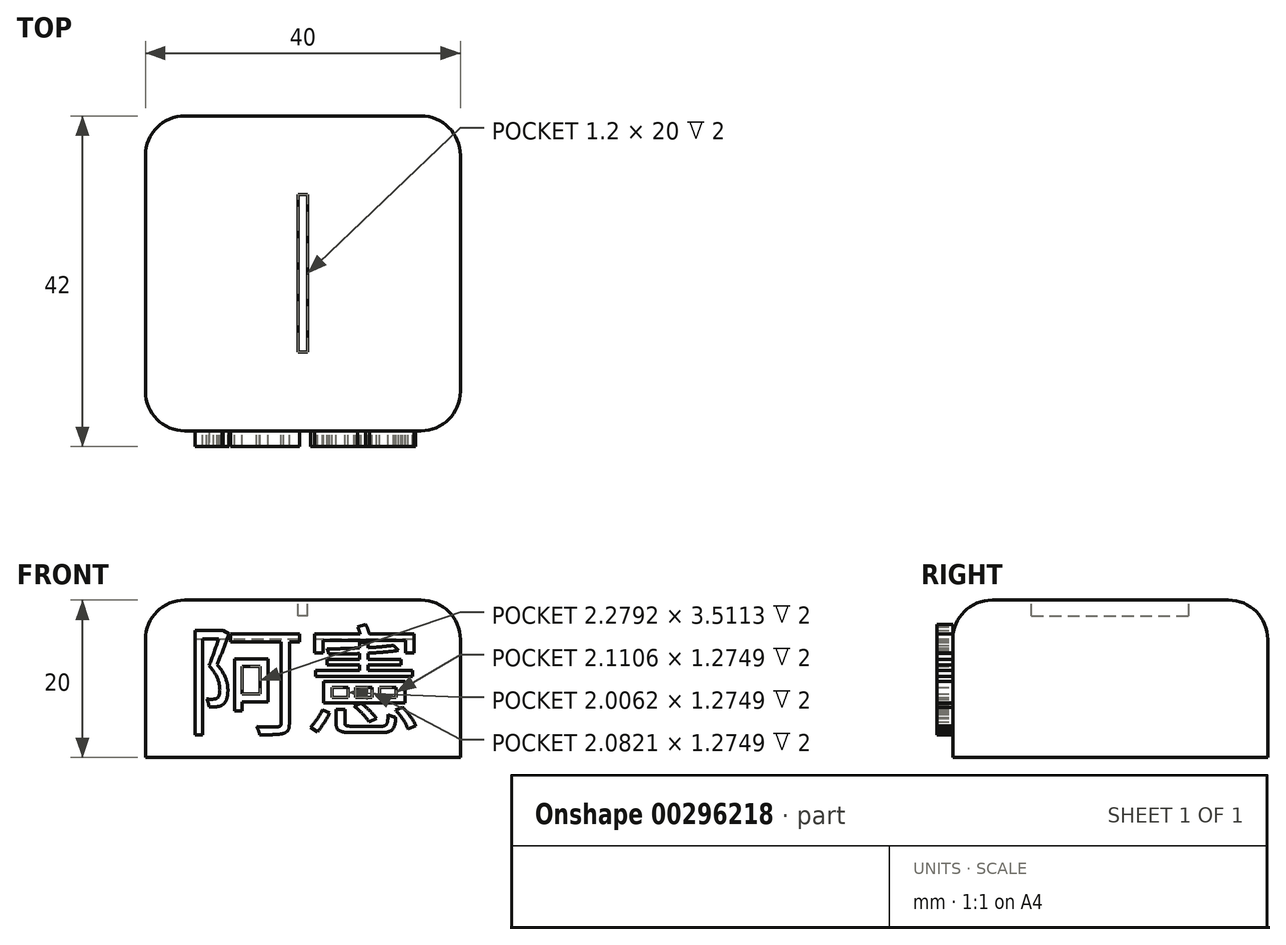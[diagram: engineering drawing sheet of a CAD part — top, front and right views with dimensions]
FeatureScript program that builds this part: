
annotation { "Feature Type Name" : "Feature", "Feature Type Description" : "" }
export const myFeature = defineFeature(function(context is Context, id is Id, definition is map)
    precondition{}
    {
        {
            var Q0;
            Q0=qCreatedBy(makeId("Top.planeOp"),FACE);
            var sketch = newSketch(context, id + "F0", { "sketchPlane" : qUnion([Q0])});
            skLineSegment(sketch, "E0.bottom", {"start": v(20, -20) * mm, "end": v(-20, -20) * mm});
            skLineSegment(sketch, "E0.top", {"start": v(20, 20) * mm, "end": v(-20, 20) * mm});
            skLineSegment(sketch, "E0.left", {"start": v(20, -20) * mm, "end": v(20, 20) * mm});
            skLineSegment(sketch, "E0.right", {"start": v(-20, -20) * mm, "end": v(-20, 20) * mm});
            skPoint(sketch, "E0.middle", {"position": v(0, 0) * mm});
            skLineSegment(sketch, "E1.bottom", {"start": v(0.6, -10) * mm, "end": v(-0.6, -10) * mm});
            skLineSegment(sketch, "E1.top", {"start": v(0.6, 10) * mm, "end": v(-0.6, 10) * mm});
            skLineSegment(sketch, "E1.left", {"start": v(0.6, -10) * mm, "end": v(0.6, 10) * mm});
            skLineSegment(sketch, "E1.right", {"start": v(-0.6, -10) * mm, "end": v(-0.6, 10) * mm});
            skSolve(sketch);
        }
        {
            var Q0;
            Q0=makeQuery(id+"F0.imprint","IMPRINT",FACE,{"disambiguationData":[TD([[makeQuery(id+"F0.imprint","IMPRINT",EDGE,{"derivedFrom":sQuery(id+"F0.wireOp",EDGE,"E0.bottom")}),-1.0]])]});
            var Q1;
            Q1=makeQuery(id+"F0.imprint","IMPRINT",FACE,{"disambiguationData":[TD([[makeQuery(id+"F0.imprint","IMPRINT",EDGE,{"derivedFrom":sQuery(id+"F0.wireOp",EDGE,"E1.bottom")}),-1.0]])]});
            extrude(context, id + "F1", {"entities" : qUnion([Q0, Q1]), "oppositeDirection" : true, "depth" : 20 * mm});
        }
        {
            var Q0;
            Q0=makeQuery(id+"F0.imprint","IMPRINT",FACE,{"disambiguationData":[TD([[makeQuery(id+"F0.imprint","IMPRINT",EDGE,{"derivedFrom":sQuery(id+"F0.wireOp",EDGE,"E1.bottom")}),-1.0]])]});
            extrude(context, id + "F2", {"entities" : qUnion([Q0]), "operationType" : NewBodyOperationType.REMOVE, "oppositeDirection" : true, "depth" : 2 * mm});
        }
        {
            var Q0;
            Q0=makeQuery(id+"F2.boolean.opBoolean","COPY",EDGE,{"derivedFrom":makeQuery(id+"F2.opExtrude","CAP_EDGE",EDGE,{"disambiguationData":[OSD([sQuery(id+"F0.wireOp",EDGE,"E1.left")])],"isStart":true})});
            var Q1;
            Q1=makeQuery(id+"F2.boolean.opBoolean","COPY",EDGE,{"derivedFrom":makeQuery(id+"F2.opExtrude","CAP_EDGE",EDGE,{"disambiguationData":[OSD([sQuery(id+"F0.wireOp",EDGE,"E1.right")])],"isStart":true})});
            var Q2;
            Q2=makeQuery(id+"F1.opExtrude","SWEPT_EDGE",EDGE,{"disambiguationData":[OSD([sQuery(id+"F0.wireOp",EDGE,"E0.bottom"),sQuery(id+"F0.wireOp",EDGE,"E0.left")])]});
            var Q3;
            Q3=makeQuery(id+"F1.opExtrude","SWEPT_EDGE",EDGE,{"disambiguationData":[OSD([sQuery(id+"F0.wireOp",EDGE,"E0.top"),sQuery(id+"F0.wireOp",EDGE,"E0.left")])]});
            var Q4;
            Q4=makeQuery(id+"F1.opExtrude","CAP_EDGE",EDGE,{"disambiguationData":[OSD([sQuery(id+"F0.wireOp",EDGE,"E0.left")])],"isStart":true});
            var Q5;
            Q5=makeQuery(id+"F1.opExtrude","SWEPT_EDGE",EDGE,{"disambiguationData":[OSD([sQuery(id+"F0.wireOp",EDGE,"E0.bottom"),sQuery(id+"F0.wireOp",EDGE,"E0.right")])]});
            var Q6;
            Q6=makeQuery(id+"F1.opExtrude","SWEPT_EDGE",EDGE,{"disambiguationData":[OSD([sQuery(id+"F0.wireOp",EDGE,"E0.top"),sQuery(id+"F0.wireOp",EDGE,"E0.right")])]});
            var Q7;
            Q7=makeQuery(id+"F1.opExtrude","CAP_EDGE",EDGE,{"disambiguationData":[OSD([sQuery(id+"F0.wireOp",EDGE,"E0.top")])],"isStart":true});
            var Q8;
            Q8=makeQuery(id+"F1.opExtrude","CAP_EDGE",EDGE,{"disambiguationData":[OSD([sQuery(id+"F0.wireOp",EDGE,"E0.right")])],"isStart":true});
            var Q9;
            Q9=makeQuery(id+"F1.opExtrude","CAP_EDGE",EDGE,{"disambiguationData":[OSD([sQuery(id+"F0.wireOp",EDGE,"E0.bottom")])],"isStart":true});
            fillet(context, id + "F3", {"entities" : qUnion([Q0, Q1, Q2, Q3, Q4, Q5, Q6, Q7, Q8, Q9]), "radius" : 5 * mm, "tangentPropagation" : true, "allowEdgeOverflow" : false});
        }
        {
            var Q0;
            Q0=makeQuery(id+"F1.opExtrude","SWEPT_FACE",FACE,{"disambiguationData":[OSD([sQuery(id+"F0.wireOp",EDGE,"E0.bottom")])]});
            var sketch = newSketch(context, id + "F4", { "sketchPlane" : qUnion([Q0])});
            skText(sketch, "E2", { "text": "阿憲", "fontName": "NotoSansCJKtc-Regular.otf"});
            const initialGuessF4  = {"E2": [-0.015, -0.01594, 1, 0, 0.01094]};
            skSetInitialGuess(sketch, initialGuessF4);
            skSolve(sketch);
        }
        {
            var Q0;
            Q0=makeQuery(id+"F4.imprint","IMPRINT",FACE,{"disambiguationData":[TD([[makeQuery(id+"F4.imprint","IMPRINT",EDGE,{"derivedFrom":sQuery(id+"F4.wireOp",EDGE,"E2.sketch_text.stroke-18")}),1.0]])]});
            var Q1;
            {var subQ7=sQuery(id+"F4.wireOp",EDGE,"E2.sketch_text.stroke-30");Q1=makeQuery(id+"F4.imprint","IMPRINT",FACE,{"disambiguationData":[TD([[makeQuery(id+"F4.imprint","IMPRINT",EDGE,{"derivedFrom":subQ7}),1.0]])]});}
            var Q2;
            {var subQ0=sQuery(id+"F4.wireOp",EDGE,"E2.sketch_text.stroke-28");Q2=makeQuery(id+"F4.imprint","IMPRINT",FACE,{"disambiguationData":[TD([[makeQuery(id+"F4.imprint","IMPRINT",EDGE,{"derivedFrom":subQ0}),1.0]])]});}
            var Q3;
            Q3=makeQuery(id+"F4.imprint","IMPRINT",FACE,{"disambiguationData":[TD([[makeQuery(id+"F4.imprint","IMPRINT",EDGE,{"derivedFrom":sQuery(id+"F4.wireOp",EDGE,"E2.sketch_text.stroke-0")}),1.0]])]});
            var Q4;
            {var subQ7=sQuery(id+"F4.wireOp",EDGE,"E2.sketch_text.stroke-7");Q4=makeQuery(id+"F4.imprint","IMPRINT",FACE,{"disambiguationData":[TD([[makeQuery(id+"F4.imprint","IMPRINT",EDGE,{"derivedFrom":subQ7}),1.0]])]});}
            var Q5;
            {var subQ0=sQuery(id+"F4.wireOp",EDGE,"E2.sketch_text.stroke-3");Q5=makeQuery(id+"F4.imprint","IMPRINT",FACE,{"disambiguationData":[TD([[makeQuery(id+"F4.imprint","IMPRINT",EDGE,{"derivedFrom":subQ0}),1.0]])]});}
            var Q6;
            {var subQ0=sQuery(id+"F4.wireOp",EDGE,"E2.sketch_text.stroke-44");Q6=makeQuery(id+"F4.imprint","IMPRINT",FACE,{"disambiguationData":[TD([[makeQuery(id+"F4.imprint","IMPRINT",EDGE,{"derivedFrom":subQ0}),1.0]])]});}
            var Q7;
            Q7=makeQuery(id+"F4.imprint","IMPRINT",FACE,{"disambiguationData":[TD([[makeQuery(id+"F4.imprint","IMPRINT",EDGE,{"derivedFrom":sQuery(id+"F4.wireOp",EDGE,"E2.sketch_text.stroke-72")}),1.0]])]});
            var Q8;
            Q8=makeQuery(id+"F4.imprint","IMPRINT",FACE,{"disambiguationData":[TD([[makeQuery(id+"F4.imprint","IMPRINT",EDGE,{"derivedFrom":sQuery(id+"F4.wireOp",EDGE,"E2.sketch_text.stroke-40")}),1.0]])]});
            var Q9;
            Q9=makeQuery(id+"F4.imprint","IMPRINT",FACE,{"disambiguationData":[TD([[makeQuery(id+"F4.imprint","IMPRINT",EDGE,{"derivedFrom":sQuery(id+"F4.wireOp",EDGE,"E2.sketch_text.stroke-52")}),1.0]])]});
            var Q10;
            Q10=makeQuery(id+"F4.imprint","IMPRINT",FACE,{"disambiguationData":[TD([[makeQuery(id+"F4.imprint","IMPRINT",EDGE,{"derivedFrom":sQuery(id+"F4.wireOp",EDGE,"E2.sketch_text.stroke-68")}),1.0]])]});
            var Q11;
            Q11=makeQuery(id+"F4.imprint","IMPRINT",FACE,{"disambiguationData":[TD([[makeQuery(id+"F4.imprint","IMPRINT",EDGE,{"derivedFrom":sQuery(id+"F4.wireOp",EDGE,"E2.sketch_text.stroke-100")}),1.0]])]});
            var Q12;
            Q12=makeQuery(id+"F4.imprint","IMPRINT",FACE,{"disambiguationData":[TD([[makeQuery(id+"F4.imprint","IMPRINT",EDGE,{"derivedFrom":sQuery(id+"F4.wireOp",EDGE,"E2.sketch_text.stroke-96")}),1.0]])]});
            var Q13;
            Q13=makeQuery(id+"F4.imprint","IMPRINT",FACE,{"disambiguationData":[TD([[makeQuery(id+"F4.imprint","IMPRINT",EDGE,{"derivedFrom":sQuery(id+"F4.wireOp",EDGE,"E2.sketch_text.stroke-110")}),1.0]])]});
            extrude(context, id + "F5", {"entities" : qUnion([Q0, Q1, Q2, Q3, Q4, Q5, Q6, Q7, Q8, Q9, Q10, Q11, Q12, Q13]), "operationType" : NewBodyOperationType.ADD, "depth" : 2 * mm});
        }
    });
